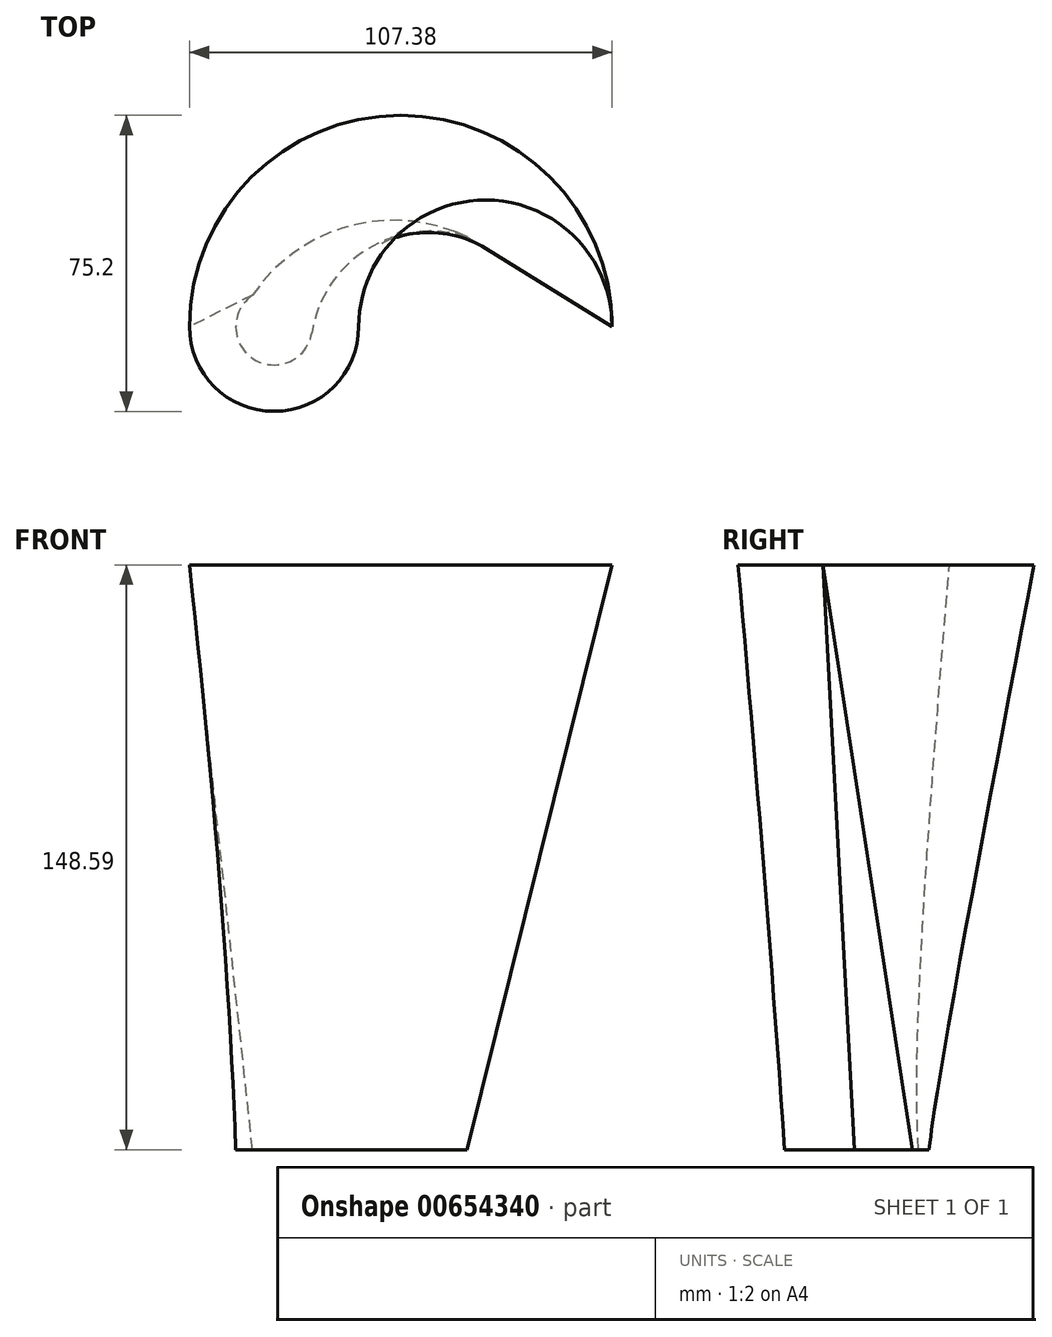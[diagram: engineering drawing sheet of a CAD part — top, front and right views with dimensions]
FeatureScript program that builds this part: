
annotation { "Feature Type Name" : "Feature", "Feature Type Description" : "" }
export const myFeature = defineFeature(function(context is Context, id is Id, definition is map)
    precondition{}
    {
        {
            var Q0;
            Q0=qCreatedBy(makeId("Top.planeOp"),FACE);
            var sketch = newSketch(context, id + "F0", { "sketchPlane" : qUnion([Q0])});
            skCircle(sketch, "E0", {"center": v(0, 0) * mm, "radius": 9.72 * mm});
            skArc(sketch, "E1", {"start": v(49.01, 22.83) * mm, "mid": v(19.04, 25.5) * mm, "end": v(-5.47, 8.04) * mm});
            skArc(sketch, "E2", {"start": v(49.01, 22.83) * mm, "mid": v(23.72, 19.7) * mm, "end": v(9.6, -1.52) * mm});
            skSolve(sketch);
        }
        {
            var Q0;
            Q0=qCreatedBy(makeId("Top.planeOp"),FACE);
            cPlane(context, id + "F1", {"entities" : qUnion([Q0]), "cplaneType" : CPlaneType.OFFSET, "offset" : 148.6 * mm, "width" : 152.4 * mm, "height" : 152.4 * mm});
        }
        {
            var Q0;
            Q0=qCreatedBy(id+"F1.planeOp",FACE);
            var sketch = newSketch(context, id + "F2", { "sketchPlane" : qUnion([Q0])});
            skCircle(sketch, "E3", {"center": v(0, 0) * mm, "radius": 21.5 * mm});
            skArc(sketch, "E4", {"start": v(85.87, 0) * mm, "mid": v(53.69, 32.18) * mm, "end": v(21.5, 0) * mm});
            skArc(sketch, "E5", {"start": v(85.87, 0) * mm, "mid": v(32.18, 53.69) * mm, "end": v(-21.5, 0) * mm});
            skSolve(sketch);
        }
        {
            var Q0;
            Q0 = qSketchRegion(id + "F0", true);
            var Q1;
            Q1 = qSketchRegion(id + "F2", true);
            loft(context, id + "F3", {"sheetProfilesArray" : [{ "sheetProfileEntities" : qUnion([Q0]) }, { "sheetProfileEntities" : qUnion([Q1]) }]});
        }
    });
